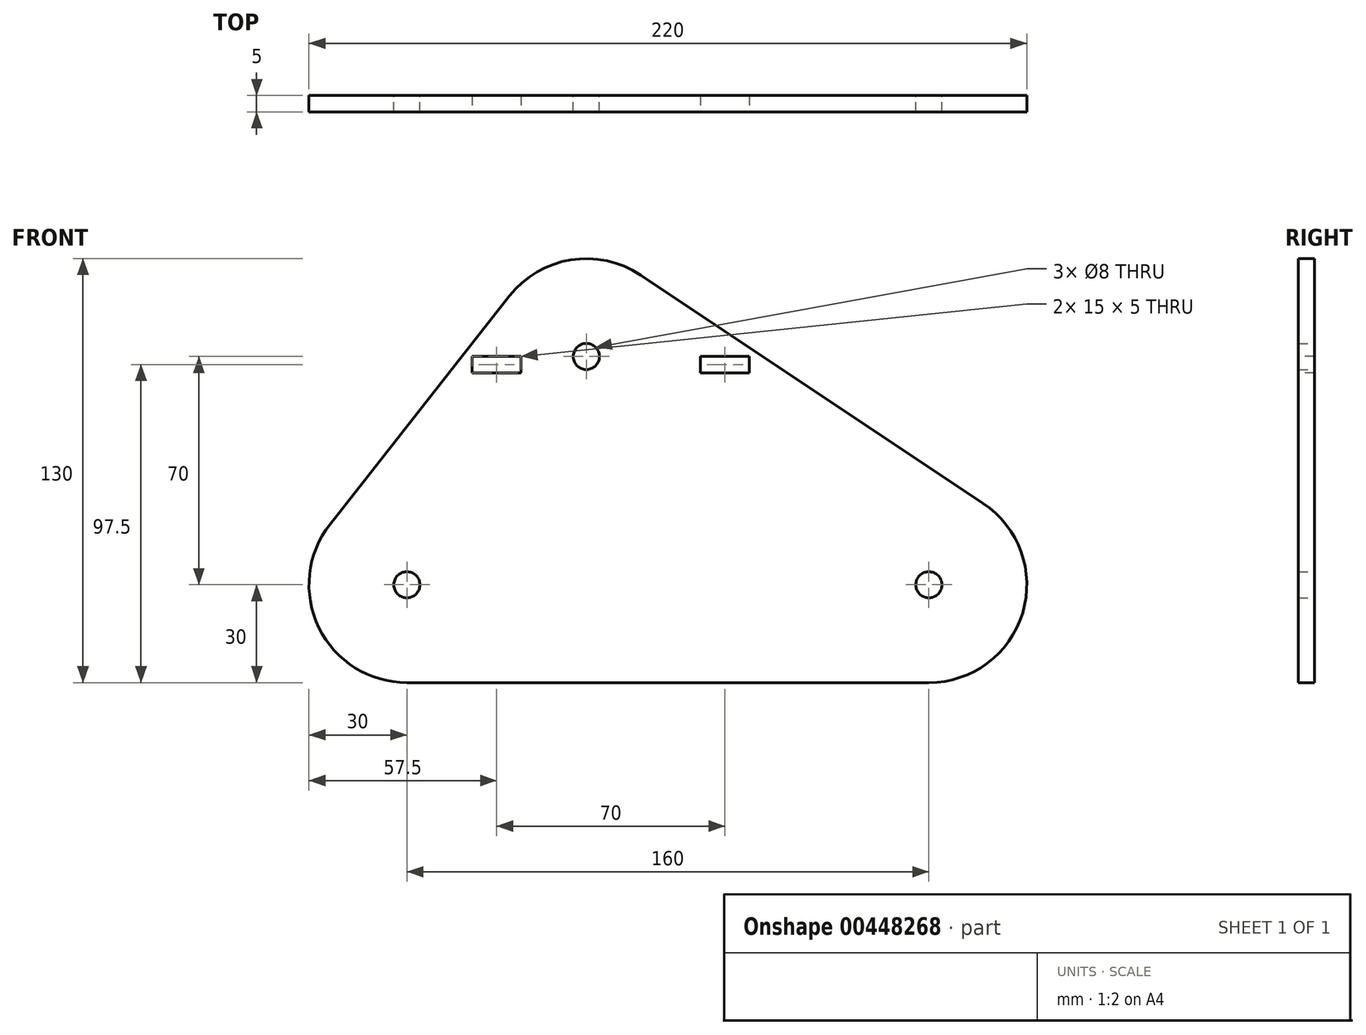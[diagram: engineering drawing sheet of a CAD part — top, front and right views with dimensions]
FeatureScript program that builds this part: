
annotation { "Feature Type Name" : "Feature", "Feature Type Description" : "" }
export const myFeature = defineFeature(function(context is Context, id is Id, definition is map)
    precondition{}
    {
        {
            var Q0;
            Q0=qCreatedBy(makeId("Front.planeOp"),FACE);
            var sketch = newSketch(context, id + "F0", { "sketchPlane" : qUnion([Q0])});
            skCircle(sketch, "E0", {"center": v(0, 70) * mm, "radius": 30 * mm, "construction": true});
            skCircle(sketch, "E1", {"center": v(-55, 0) * mm, "radius": 30 * mm, "construction": true});
            skCircle(sketch, "E2", {"center": v(105, 0) * mm, "radius": 30 * mm, "construction": true});
            skLineSegment(sketch, "E3", {"start": v(-55, 0) * mm, "end": v(105, 0) * mm, "construction": true});
            skLineSegment(sketch, "E4", {"start": v(0, 70) * mm, "end": v(0, 0) * mm, "construction": true});
            skArc(sketch, "E5", {"start": v(-78.59, 18.53) * mm, "mid": v(-81.98, -13.11) * mm, "end": v(-55, -30) * mm});
            skArc(sketch, "E6", {"start": v(16.64, 94.96) * mm, "mid": v(-4.73, 99.62) * mm, "end": v(-23.59, 88.53) * mm});
            skArc(sketch, "E7", {"start": v(105, -30) * mm, "mid": v(133.71, -8.7) * mm, "end": v(121.64, 24.96) * mm});
            skLineSegment(sketch, "E8", {"start": v(-6.45, 110.35) * mm, "end": v(-116.72, -30) * mm, "construction": true});
            skLineSegment(sketch, "E9", {"start": v(-116.72, -30) * mm, "end": v(204.08, -30) * mm, "construction": true});
            skLineSegment(sketch, "E10", {"start": v(-6.45, 110.35) * mm, "end": v(204.08, -30) * mm, "construction": true});
            skLineSegment(sketch, "E11", {"start": v(-78.59, 18.53) * mm, "end": v(-23.59, 88.53) * mm});
            skLineSegment(sketch, "E12", {"start": v(16.64, 94.96) * mm, "end": v(121.64, 24.96) * mm});
            skLineSegment(sketch, "E13", {"start": v(-55, -30) * mm, "end": v(105, -30) * mm});
            skCircle(sketch, "E14", {"center": v(0, 70) * mm, "radius": 4 * mm});
            skCircle(sketch, "E15", {"center": v(-55, 0) * mm, "radius": 4 * mm});
            skCircle(sketch, "E16", {"center": v(105, 0) * mm, "radius": 4 * mm});
            skSolve(sketch);
        }
        {
            var Q0;
            Q0=makeQuery(id+"F0.imprint","IMPRINT",FACE,{"disambiguationData":[TD([[makeQuery(id+"F0.imprint","IMPRINT",EDGE,{"derivedFrom":sQuery(id+"F0.wireOp",EDGE,"E5")}),1.0]])]});
            extrude(context, id + "F1", {"entities" : qUnion([Q0]), "depth" : 5 * mm});
        }
        {
            var Q0;
            Q0=makeQuery(id+"F1.opExtrude","CAP_FACE",FACE,{"disambiguationData":[OSD([sQuery(id+"F0.wireOp",EDGE,"E5"),sQuery(id+"F0.wireOp",EDGE,"E6"),sQuery(id+"F0.wireOp",EDGE,"E7"),sQuery(id+"F0.wireOp",EDGE,"E11"),sQuery(id+"F0.wireOp",EDGE,"E12"),sQuery(id+"F0.wireOp",EDGE,"E13"),sQuery(id+"F0.wireOp",EDGE,"E14"),sQuery(id+"F0.wireOp",EDGE,"E15"),sQuery(id+"F0.wireOp",EDGE,"E16")])],"isStart":false});
            var sketch = newSketch(context, id + "F2", { "sketchPlane" : qUnion([Q0])});
            skCircle(sketch, "E17", {"center": v(0, 70) * mm, "radius": 35 * mm, "construction": true});
            skCircle(sketch, "E18", {"center": v(105, 0) * mm, "radius": 35 * mm, "construction": true});
            skCircle(sketch, "E19", {"center": v(-55, 0) * mm, "radius": 35 * mm, "construction": true});
            skLineSegment(sketch, "E20", {"start": v(-20, 112.77) * mm, "end": v(-20, -36.3) * mm, "construction": true});
            skLineSegment(sketch, "E21", {"start": v(-104.82, 70) * mm, "end": v(178.65, 70) * mm, "construction": true});
            skLineSegment(sketch, "E22", {"start": v(-105.7, 65) * mm, "end": v(180.7, 65) * mm, "construction": true});
            skLineSegment(sketch, "E23", {"start": v(-35, 119.24) * mm, "end": v(-35, -37.2) * mm, "construction": true});
            skLineSegment(sketch, "E24", {"start": v(35, 111.89) * mm, "end": v(35, -26.62) * mm, "construction": true});
            skLineSegment(sketch, "E25", {"start": v(50, 112.48) * mm, "end": v(50, -28.08) * mm, "construction": true});
            skLineSegment(sketch, "E26.bottom", {"start": v(-35, 70) * mm, "end": v(-20, 70) * mm});
            skLineSegment(sketch, "E26.top", {"start": v(-35, 65) * mm, "end": v(-20, 65) * mm});
            skLineSegment(sketch, "E26.left", {"start": v(-35, 70) * mm, "end": v(-35, 65) * mm});
            skLineSegment(sketch, "E26.right", {"start": v(-20, 70) * mm, "end": v(-20, 65) * mm});
            skLineSegment(sketch, "E27.bottom", {"start": v(35, 70) * mm, "end": v(50, 70) * mm});
            skLineSegment(sketch, "E27.top", {"start": v(35, 65) * mm, "end": v(50, 65) * mm});
            skLineSegment(sketch, "E27.left", {"start": v(35, 70) * mm, "end": v(35, 65) * mm});
            skLineSegment(sketch, "E27.right", {"start": v(50, 70) * mm, "end": v(50, 65) * mm});
            skSolve(sketch);
        }
        {
            var Q0;
            Q0=makeQuery(id+"F2.imprint","IMPRINT",FACE,{"disambiguationData":[TD([[makeQuery(id+"F2.imprint","IMPRINT",EDGE,{"derivedFrom":sQuery(id+"F2.wireOp",EDGE,"E26.bottom")}),-1.0]])]});
            var Q1;
            Q1=makeQuery(id+"F2.imprint","IMPRINT",FACE,{"disambiguationData":[TD([[makeQuery(id+"F2.imprint","IMPRINT",EDGE,{"derivedFrom":sQuery(id+"F2.wireOp",EDGE,"E27.bottom")}),-1.0]])]});
            extrude(context, id + "F3", {"entities" : qUnion([Q0, Q1]), "operationType" : NewBodyOperationType.REMOVE, "oppositeDirection" : true, "depth" : 5 * mm});
        }
    });
